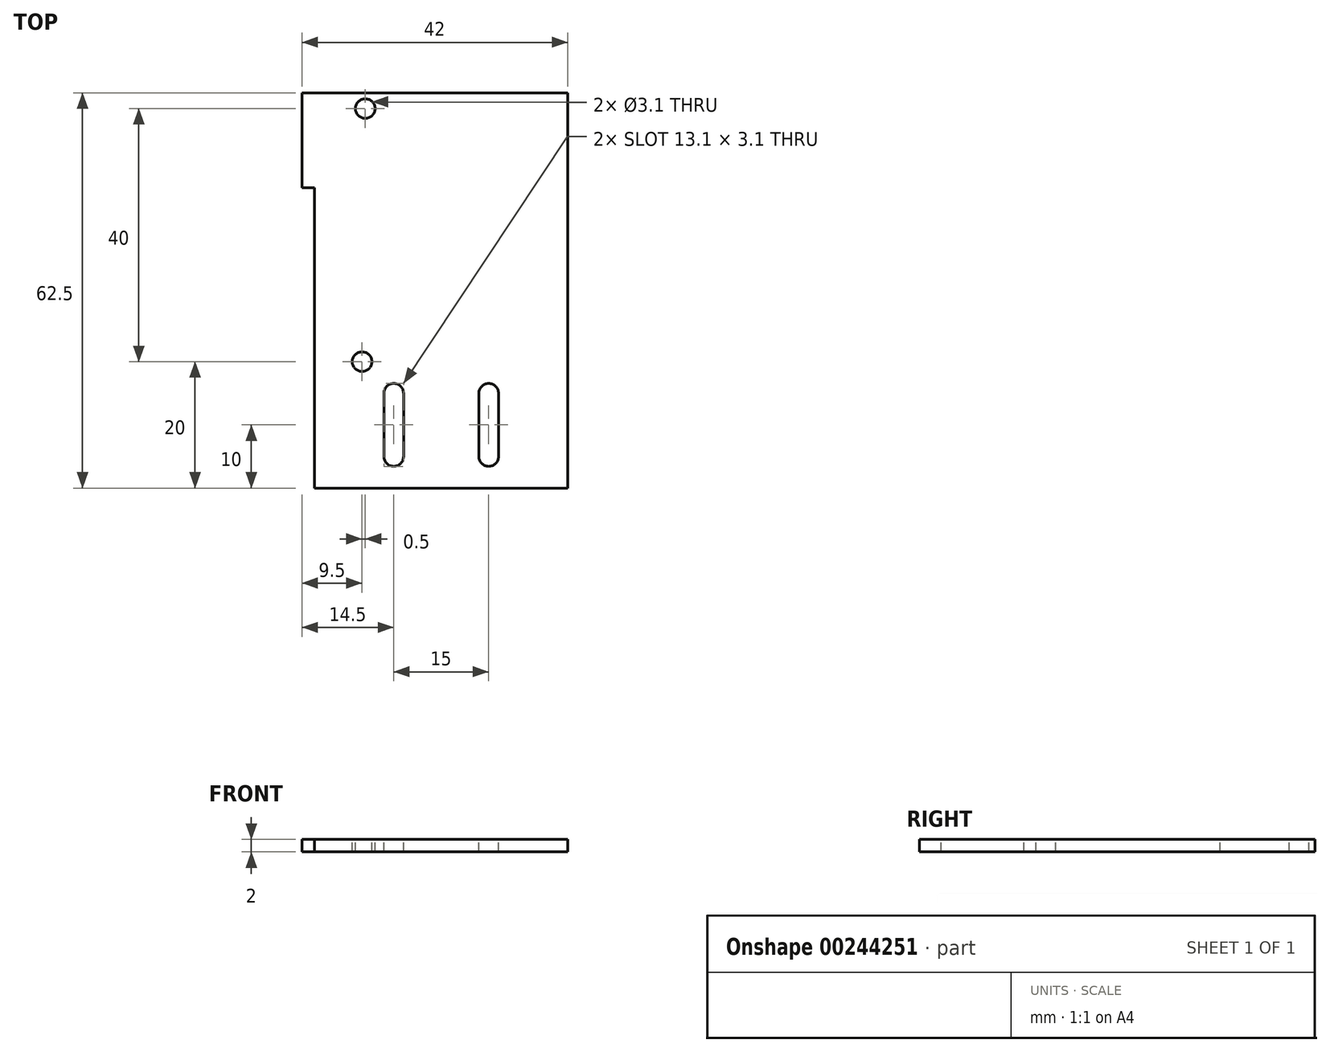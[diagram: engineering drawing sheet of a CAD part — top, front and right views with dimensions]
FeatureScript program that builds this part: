
annotation { "Feature Type Name" : "Feature", "Feature Type Description" : "" }
export const myFeature = defineFeature(function(context is Context, id is Id, definition is map)
    precondition{}
    {
        {
            var Q0;
            Q0=qCreatedBy(makeId("Top.planeOp"),FACE);
            var sketch = newSketch(context, id + "F0", { "sketchPlane" : qUnion([Q0])});
            skLineSegment(sketch, "E0.bottom", {"start": v(20, 32.5) * mm, "end": v(-20, 32.5) * mm});
            skLineSegment(sketch, "E0.top", {"start": v(20, -32.5) * mm, "end": v(-20, -32.5) * mm});
            skLineSegment(sketch, "E0.left", {"start": v(20, 32.5) * mm, "end": v(20, -32.5) * mm});
            skLineSegment(sketch, "E0.right", {"start": v(-20, 32.5) * mm, "end": v(-20, -32.5) * mm});
            skPoint(sketch, "E0.middle", {"position": v(0, 0) * mm});
            skSolve(sketch);
        }
        {
            var Q0;
            Q0=qSketchRegion(id+"F0",true);
            extrude(context, id + "F1", {"entities" : qUnion([Q0]), "depth" : 2 * mm});
        }
        {
            var Q0;
            Q0=makeQuery(id+"F1.opExtrude","CAP_FACE",FACE,{"disambiguationData":[OSD([sQuery(id+"F0.wireOp",EDGE,"E0.bottom"),sQuery(id+"F0.wireOp",EDGE,"E0.top"),sQuery(id+"F0.wireOp",EDGE,"E0.left"),sQuery(id+"F0.wireOp",EDGE,"E0.right")])],"isStart":false});
            var sketch = newSketch(context, id + "F2", { "sketchPlane" : qUnion([Q0])});
            skLineSegment(sketch, "E1", {"start": v(0, 0) * mm, "end": v(0, 20) * mm, "construction": true});
            skLineSegment(sketch, "E2", {"start": v(0, 20) * mm, "end": v(-20, 20) * mm, "construction": true});
            skLineSegment(sketch, "E3.bottom", {"start": v(-20, 12.5) * mm, "end": v(-22, 12.5) * mm});
            skLineSegment(sketch, "E3.top", {"start": v(-20, 27.5) * mm, "end": v(-22, 27.5) * mm});
            skLineSegment(sketch, "E3.left", {"start": v(-20, 12.5) * mm, "end": v(-20, 27.5) * mm});
            skLineSegment(sketch, "E3.right", {"start": v(-22, 12.5) * mm, "end": v(-22, 27.5) * mm});
            skSolve(sketch);
        }
        {
            var Q0;
            Q0=qSketchRegion(id+"F2",true);
            extrude(context, id + "F3", {"entities" : qUnion([Q0]), "operationType" : NewBodyOperationType.ADD, "oppositeDirection" : true, "depth" : 2 * mm});
        }
        {
            var Q0;
            {var subQ0=sQuery(id+"F2.wireOp",EDGE,"E3.right");var subQ1=sQuery(id+"F2.wireOp",EDGE,"E3.left");var subQ2=sQuery(id+"F2.wireOp",EDGE,"E3.top");var subQ3=sQuery(id+"F2.wireOp",EDGE,"E3.bottom");Q0=makeQuery(id+"FAu347zrFNA7xFl_1.1.FN0kvEoHNVdJmEl_1.1.F3.boolean.opBoolean","MERGE",FACE,{"derivedFrom":[makeQuery(id+"FAu347zrFNA7xFl_1.1.F3.boolean.opBoolean","MERGE",FACE,{"derivedFrom":[makeQuery(id+"FN0kvEoHNVdJmEl_1.1.F3.boolean.opBoolean","MERGE",FACE,{"derivedFrom":[makeQuery(id+"F3.boolean.opBoolean","MERGE",FACE,{"derivedFrom":[makeQuery(id+"F1.opExtrude","CAP_FACE",FACE,{"disambiguationData":[OSD([sQuery(id+"F0.wireOp",EDGE,"E0.bottom"),sQuery(id+"F0.wireOp",EDGE,"E0.top"),sQuery(id+"F0.wireOp",EDGE,"E0.left"),sQuery(id+"F0.wireOp",EDGE,"E0.right")])],"isStart":false}),makeQuery(id+"F3.opExtrude","CAP_FACE",FACE,{"disambiguationData":[OSD([subQ3,subQ2,subQ1,subQ0])],"isStart":true})]}),makeQuery(id+"FN0kvEoHNVdJmEl_1.1.F3.opExtrude","CAP_FACE",FACE,{"disambiguationData":[OSD([subQ3,subQ2,subQ1,subQ0])],"isStart":true})]}),makeQuery(id+"FAu347zrFNA7xFl_1.1.F3.opExtrude","CAP_FACE",FACE,{"disambiguationData":[OSD([subQ3,subQ2,subQ1,subQ0])],"isStart":true})]}),makeQuery(id+"FAu347zrFNA7xFl_1.1.FN0kvEoHNVdJmEl_1.1.F3.opExtrude","CAP_FACE",FACE,{"disambiguationData":[OSD([subQ3,subQ2,subQ1,subQ0])],"isStart":true})]});}
            var sketch = newSketch(context, id + "F4", { "sketchPlane" : qUnion([Q0])});
            skLineSegment(sketch, "E4", {"start": v(0, 0) * mm, "end": v(0, 25) * mm, "construction": true});
            skLineSegment(sketch, "E5", {"start": v(0, 25) * mm, "end": v(-12, 25) * mm, "construction": true});
            skCircle(sketch, "E6", {"center": v(-12, 25) * mm, "radius": 1.55 * mm});
            skSolve(sketch);
        }
        {
            var Q0;
            Q0=qSketchRegion(id+"F4",true);
            extrude(context, id + "F5", {"entities" : qUnion([Q0]), "operationType" : NewBodyOperationType.REMOVE, "endBound" : BoundingType.THROUGH_ALL, "oppositeDirection" : true, "depth" : 25 * mm});
        }
        {
            var Q0;
            {var subQ0=sQuery(id+"F2.wireOp",EDGE,"E3.right");var subQ1=sQuery(id+"F2.wireOp",EDGE,"E3.left");var subQ2=sQuery(id+"F2.wireOp",EDGE,"E3.top");var subQ3=sQuery(id+"F2.wireOp",EDGE,"E3.bottom");Q0=makeQuery(id+"FAu347zrFNA7xFl_1.1.FN0kvEoHNVdJmEl_1.1.F3.boolean.opBoolean","MERGE",FACE,{"derivedFrom":[makeQuery(id+"FAu347zrFNA7xFl_1.1.F3.boolean.opBoolean","MERGE",FACE,{"derivedFrom":[makeQuery(id+"FN0kvEoHNVdJmEl_1.1.F3.boolean.opBoolean","MERGE",FACE,{"derivedFrom":[makeQuery(id+"F3.boolean.opBoolean","MERGE",FACE,{"derivedFrom":[makeQuery(id+"F1.opExtrude","CAP_FACE",FACE,{"disambiguationData":[OSD([sQuery(id+"F0.wireOp",EDGE,"E0.bottom"),sQuery(id+"F0.wireOp",EDGE,"E0.top"),sQuery(id+"F0.wireOp",EDGE,"E0.left"),sQuery(id+"F0.wireOp",EDGE,"E0.right")])],"isStart":false}),makeQuery(id+"F3.opExtrude","CAP_FACE",FACE,{"disambiguationData":[OSD([subQ3,subQ2,subQ1,subQ0])],"isStart":true})]}),makeQuery(id+"FN0kvEoHNVdJmEl_1.1.F3.opExtrude","CAP_FACE",FACE,{"disambiguationData":[OSD([subQ3,subQ2,subQ1,subQ0])],"isStart":true})]}),makeQuery(id+"FAu347zrFNA7xFl_1.1.F3.opExtrude","CAP_FACE",FACE,{"disambiguationData":[OSD([subQ3,subQ2,subQ1,subQ0])],"isStart":true})]}),makeQuery(id+"FAu347zrFNA7xFl_1.1.FN0kvEoHNVdJmEl_1.1.F3.opExtrude","CAP_FACE",FACE,{"disambiguationData":[OSD([subQ3,subQ2,subQ1,subQ0])],"isStart":true})]});}
            var sketch = newSketch(context, id + "F6", { "sketchPlane" : qUnion([Q0])});
            skLineSegment(sketch, "E7", {"start": v(0, 0) * mm, "end": v(0, -30) * mm, "construction": true});
            skLineSegment(sketch, "E8", {"start": v(0, -30) * mm, "end": v(7.5, -30) * mm, "construction": true});
            skLineSegment(sketch, "E9", {"start": v(0, -30) * mm, "end": v(-7.5, -30) * mm, "construction": true});
            skArc(sketch, "E10", {"start": v(-9.05, -30) * mm, "mid": v(-7.5, -31.55) * mm, "end": v(-5.95, -30) * mm});
            skArc(sketch, "E11", {"start": v(5.95, -30) * mm, "mid": v(7.5, -31.55) * mm, "end": v(9.05, -30) * mm});
            skLineSegment(sketch, "E12", {"start": v(-7.5, -30) * mm, "end": v(-7.5, -20) * mm, "construction": true});
            skLineSegment(sketch, "E13", {"start": v(7.5, -30) * mm, "end": v(7.5, -20) * mm, "construction": true});
            skArc(sketch, "E14", {"start": v(9.05, -20) * mm, "mid": v(7.5, -18.45) * mm, "end": v(5.95, -20) * mm});
            skArc(sketch, "E15", {"start": v(-5.95, -20) * mm, "mid": v(-7.5, -18.45) * mm, "end": v(-9.05, -20) * mm});
            skLineSegment(sketch, "E16", {"start": v(-5.95, -20) * mm, "end": v(-9.05, -20) * mm, "construction": true});
            skLineSegment(sketch, "E17", {"start": v(5.95, -20) * mm, "end": v(9.05, -20) * mm, "construction": true});
            skLineSegment(sketch, "E18", {"start": v(9.05, -30) * mm, "end": v(7.5, -30) * mm, "construction": true});
            skLineSegment(sketch, "E19", {"start": v(-7.5, -30) * mm, "end": v(-9.05, -30) * mm, "construction": true});
            skLineSegment(sketch, "E20", {"start": v(-9.05, -20) * mm, "end": v(-9.05, -30) * mm});
            skLineSegment(sketch, "E21", {"start": v(-7.5, -30) * mm, "end": v(-5.95, -30) * mm, "construction": true});
            skLineSegment(sketch, "E22", {"start": v(7.5, -30) * mm, "end": v(5.95, -30) * mm, "construction": true});
            skLineSegment(sketch, "E23", {"start": v(5.95, -20) * mm, "end": v(5.95, -30) * mm});
            skLineSegment(sketch, "E24", {"start": v(9.05, -20) * mm, "end": v(9.05, -30) * mm});
            skLineSegment(sketch, "E25", {"start": v(-5.95, -20) * mm, "end": v(-5.95, -30) * mm});
            skSolve(sketch);
        }
        {
            var Q0;
            Q0=qSketchRegion(id+"F6",true);
            extrude(context, id + "F7", {"entities" : qUnion([Q0]), "operationType" : NewBodyOperationType.REMOVE, "endBound" : BoundingType.THROUGH_ALL, "oppositeDirection" : true, "depth" : 25 * mm});
        }
        {
            var Q0;
            {var subQ0=sQuery(id+"F2.wireOp",EDGE,"E3.right");var subQ1=sQuery(id+"F2.wireOp",EDGE,"E3.left");var subQ2=sQuery(id+"F2.wireOp",EDGE,"E3.top");var subQ3=sQuery(id+"F2.wireOp",EDGE,"E3.bottom");Q0=makeQuery(id+"FAu347zrFNA7xFl_1.1.FN0kvEoHNVdJmEl_1.1.F3.boolean.opBoolean","MERGE",FACE,{"derivedFrom":[makeQuery(id+"FAu347zrFNA7xFl_1.1.F3.boolean.opBoolean","MERGE",FACE,{"derivedFrom":[makeQuery(id+"FN0kvEoHNVdJmEl_1.1.F3.boolean.opBoolean","MERGE",FACE,{"derivedFrom":[makeQuery(id+"F3.boolean.opBoolean","MERGE",FACE,{"derivedFrom":[makeQuery(id+"F1.opExtrude","CAP_FACE",FACE,{"disambiguationData":[OSD([sQuery(id+"F0.wireOp",EDGE,"E0.bottom"),sQuery(id+"F0.wireOp",EDGE,"E0.top"),sQuery(id+"F0.wireOp",EDGE,"E0.left"),sQuery(id+"F0.wireOp",EDGE,"E0.right")])],"isStart":false}),makeQuery(id+"F3.opExtrude","CAP_FACE",FACE,{"disambiguationData":[OSD([subQ3,subQ2,subQ1,subQ0])],"isStart":true})]}),makeQuery(id+"FN0kvEoHNVdJmEl_1.1.F3.opExtrude","CAP_FACE",FACE,{"disambiguationData":[OSD([subQ3,subQ2,subQ1,subQ0])],"isStart":true})]}),makeQuery(id+"FAu347zrFNA7xFl_1.1.F3.opExtrude","CAP_FACE",FACE,{"disambiguationData":[OSD([subQ3,subQ2,subQ1,subQ0])],"isStart":true})]}),makeQuery(id+"FAu347zrFNA7xFl_1.1.FN0kvEoHNVdJmEl_1.1.F3.opExtrude","CAP_FACE",FACE,{"disambiguationData":[OSD([subQ3,subQ2,subQ1,subQ0])],"isStart":true})]});}
            var sketch = newSketch(context, id + "F8", { "sketchPlane" : qUnion([Q0])});
            skLineSegment(sketch, "E26.bottom", {"start": v(-20, -32.5) * mm, "end": v(20, -32.5) * mm});
            skLineSegment(sketch, "E26.top", {"start": v(-20, -35) * mm, "end": v(20, -35) * mm});
            skLineSegment(sketch, "E26.left", {"start": v(-20, -32.5) * mm, "end": v(-20, -35) * mm});
            skLineSegment(sketch, "E26.right", {"start": v(20, -32.5) * mm, "end": v(20, -35) * mm});
            skSolve(sketch);
        }
        {
            var Q0;
            Q0=qSketchRegion(id+"F8",true);
            var Q1;
            {var subQ0=sQuery(id+"F2.wireOp",EDGE,"E3.right");var subQ1=sQuery(id+"F2.wireOp",EDGE,"E3.left");var subQ2=sQuery(id+"F2.wireOp",EDGE,"E3.top");var subQ3=sQuery(id+"F2.wireOp",EDGE,"E3.bottom");Q1=makeQuery(id+"FAu347zrFNA7xFl_1.1.FN0kvEoHNVdJmEl_1.1.F3.boolean.opBoolean","MERGE",FACE,{"derivedFrom":[makeQuery(id+"FAu347zrFNA7xFl_1.1.F3.boolean.opBoolean","MERGE",FACE,{"derivedFrom":[makeQuery(id+"FN0kvEoHNVdJmEl_1.1.F3.boolean.opBoolean","MERGE",FACE,{"derivedFrom":[makeQuery(id+"F3.boolean.opBoolean","MERGE",FACE,{"derivedFrom":[makeQuery(id+"F1.opExtrude","CAP_FACE",FACE,{"disambiguationData":[OSD([sQuery(id+"F0.wireOp",EDGE,"E0.bottom"),sQuery(id+"F0.wireOp",EDGE,"E0.top"),sQuery(id+"F0.wireOp",EDGE,"E0.left"),sQuery(id+"F0.wireOp",EDGE,"E0.right")])],"isStart":true}),makeQuery(id+"F3.opExtrude","CAP_FACE",FACE,{"disambiguationData":[OSD([subQ3,subQ2,subQ1,subQ0])],"isStart":false})]}),makeQuery(id+"FN0kvEoHNVdJmEl_1.1.F3.opExtrude","CAP_FACE",FACE,{"disambiguationData":[OSD([subQ3,subQ2,subQ1,subQ0])],"isStart":false})]}),makeQuery(id+"FAu347zrFNA7xFl_1.1.F3.opExtrude","CAP_FACE",FACE,{"disambiguationData":[OSD([subQ3,subQ2,subQ1,subQ0])],"isStart":false})]}),makeQuery(id+"FAu347zrFNA7xFl_1.1.FN0kvEoHNVdJmEl_1.1.F3.opExtrude","CAP_FACE",FACE,{"disambiguationData":[OSD([subQ3,subQ2,subQ1,subQ0])],"isStart":false})]});}
            extrude(context, id + "F9", {"entities" : qUnion([Q0]), "operationType" : NewBodyOperationType.ADD, "endBound" : BoundingType.UP_TO_SURFACE, "oppositeDirection" : true, "endBoundEntityFace" : qUnion([Q1]), "depth" : 2 * mm});
        }
        {
            var Q0;
            {var subQ0=sQuery(id+"F2.wireOp",EDGE,"E3.right");var subQ1=sQuery(id+"F2.wireOp",EDGE,"E3.left");var subQ2=sQuery(id+"F2.wireOp",EDGE,"E3.top");var subQ3=sQuery(id+"F2.wireOp",EDGE,"E3.bottom");Q0=makeQuery(id+"F9.boolean.opBoolean","MERGE",FACE,{"derivedFrom":[makeQuery(id+"FAu347zrFNA7xFl_1.1.FN0kvEoHNVdJmEl_1.1.F3.boolean.opBoolean","MERGE",FACE,{"derivedFrom":[makeQuery(id+"FAu347zrFNA7xFl_1.1.F3.boolean.opBoolean","MERGE",FACE,{"derivedFrom":[makeQuery(id+"FN0kvEoHNVdJmEl_1.1.F3.boolean.opBoolean","MERGE",FACE,{"derivedFrom":[makeQuery(id+"F3.boolean.opBoolean","MERGE",FACE,{"derivedFrom":[makeQuery(id+"F1.opExtrude","CAP_FACE",FACE,{"disambiguationData":[OSD([sQuery(id+"F0.wireOp",EDGE,"E0.bottom"),sQuery(id+"F0.wireOp",EDGE,"E0.top"),sQuery(id+"F0.wireOp",EDGE,"E0.left"),sQuery(id+"F0.wireOp",EDGE,"E0.right")])],"isStart":false}),makeQuery(id+"F3.opExtrude","CAP_FACE",FACE,{"disambiguationData":[OSD([subQ3,subQ2,subQ1,subQ0])],"isStart":true})]}),makeQuery(id+"FN0kvEoHNVdJmEl_1.1.F3.opExtrude","CAP_FACE",FACE,{"disambiguationData":[OSD([subQ3,subQ2,subQ1,subQ0])],"isStart":true})]}),makeQuery(id+"FAu347zrFNA7xFl_1.1.F3.opExtrude","CAP_FACE",FACE,{"disambiguationData":[OSD([subQ3,subQ2,subQ1,subQ0])],"isStart":true})]}),makeQuery(id+"FAu347zrFNA7xFl_1.1.FN0kvEoHNVdJmEl_1.1.F3.opExtrude","CAP_FACE",FACE,{"disambiguationData":[OSD([subQ3,subQ2,subQ1,subQ0])],"isStart":true})]}),makeQuery(id+"F9.opExtrude","CAP_FACE",FACE,{"disambiguationData":[OSD([sQuery(id+"F8.wireOp",EDGE,"E26.bottom"),sQuery(id+"F8.wireOp",EDGE,"E26.top"),sQuery(id+"F8.wireOp",EDGE,"E26.left"),sQuery(id+"F8.wireOp",EDGE,"E26.right")])],"isStart":true})]});}
            var sketch = newSketch(context, id + "F10", { "sketchPlane" : qUnion([Q0])});
            skCircle(sketch, "E27", {"center": v(-12.5, -15) * mm, "radius": 1.55 * mm});
            skLineSegment(sketch, "E28", {"start": v(-12.5, -15) * mm, "end": v(0, -15) * mm, "construction": true});
            skLineSegment(sketch, "E29", {"start": v(0, -15) * mm, "end": v(0, 0) * mm, "construction": true});
            skSolve(sketch);
        }
        {
            var Q0;
            Q0=qSketchRegion(id+"F10",true);
            extrude(context, id + "F11", {"entities" : qUnion([Q0]), "operationType" : NewBodyOperationType.REMOVE, "endBound" : BoundingType.THROUGH_ALL, "oppositeDirection" : true, "depth" : 25 * mm});
        }
        {
            var Q0;
            {var subQ0=sQuery(id+"F2.wireOp",EDGE,"E3.right");var subQ1=sQuery(id+"F2.wireOp",EDGE,"E3.left");var subQ2=sQuery(id+"F2.wireOp",EDGE,"E3.top");var subQ3=sQuery(id+"F2.wireOp",EDGE,"E3.bottom");Q0=makeQuery(id+"F9.boolean.opBoolean","MERGE",FACE,{"derivedFrom":[makeQuery(id+"FAu347zrFNA7xFl_1.1.FN0kvEoHNVdJmEl_1.1.F3.boolean.opBoolean","MERGE",FACE,{"derivedFrom":[makeQuery(id+"FAu347zrFNA7xFl_1.1.F3.boolean.opBoolean","MERGE",FACE,{"derivedFrom":[makeQuery(id+"FN0kvEoHNVdJmEl_1.1.F3.boolean.opBoolean","MERGE",FACE,{"derivedFrom":[makeQuery(id+"F3.boolean.opBoolean","MERGE",FACE,{"derivedFrom":[makeQuery(id+"F1.opExtrude","CAP_FACE",FACE,{"disambiguationData":[OSD([sQuery(id+"F0.wireOp",EDGE,"E0.bottom"),sQuery(id+"F0.wireOp",EDGE,"E0.top"),sQuery(id+"F0.wireOp",EDGE,"E0.left"),sQuery(id+"F0.wireOp",EDGE,"E0.right")])],"isStart":false}),makeQuery(id+"F3.opExtrude","CAP_FACE",FACE,{"disambiguationData":[OSD([subQ3,subQ2,subQ1,subQ0])],"isStart":true})]}),makeQuery(id+"FN0kvEoHNVdJmEl_1.1.F3.opExtrude","CAP_FACE",FACE,{"disambiguationData":[OSD([subQ3,subQ2,subQ1,subQ0])],"isStart":true})]}),makeQuery(id+"FAu347zrFNA7xFl_1.1.F3.opExtrude","CAP_FACE",FACE,{"disambiguationData":[OSD([subQ3,subQ2,subQ1,subQ0])],"isStart":true})]}),makeQuery(id+"FAu347zrFNA7xFl_1.1.FN0kvEoHNVdJmEl_1.1.F3.opExtrude","CAP_FACE",FACE,{"disambiguationData":[OSD([subQ3,subQ2,subQ1,subQ0])],"isStart":true})]}),makeQuery(id+"F9.opExtrude","CAP_FACE",FACE,{"disambiguationData":[OSD([sQuery(id+"F8.wireOp",EDGE,"E26.bottom"),sQuery(id+"F8.wireOp",EDGE,"E26.top"),sQuery(id+"F8.wireOp",EDGE,"E26.left"),sQuery(id+"F8.wireOp",EDGE,"E26.right")])],"isStart":true})]});}
            var sketch = newSketch(context, id + "F12", { "sketchPlane" : qUnion([Q0])});
            skLineSegment(sketch, "E30.bottom", {"start": v(-20, 27.5) * mm, "end": v(20, 27.5) * mm});
            skLineSegment(sketch, "E30.top", {"start": v(-20, 32.5) * mm, "end": v(20, 32.5) * mm});
            skLineSegment(sketch, "E30.left", {"start": v(-20, 27.5) * mm, "end": v(-20, 32.5) * mm});
            skLineSegment(sketch, "E30.right", {"start": v(20, 27.5) * mm, "end": v(20, 32.5) * mm});
            skSolve(sketch);
        }
        {
            var Q0;
            Q0=qSketchRegion(id+"F12",true);
            extrude(context, id + "F13", {"entities" : qUnion([Q0]), "operationType" : NewBodyOperationType.REMOVE, "oppositeDirection" : true, "depth" : 25 * mm});
        }
    });
